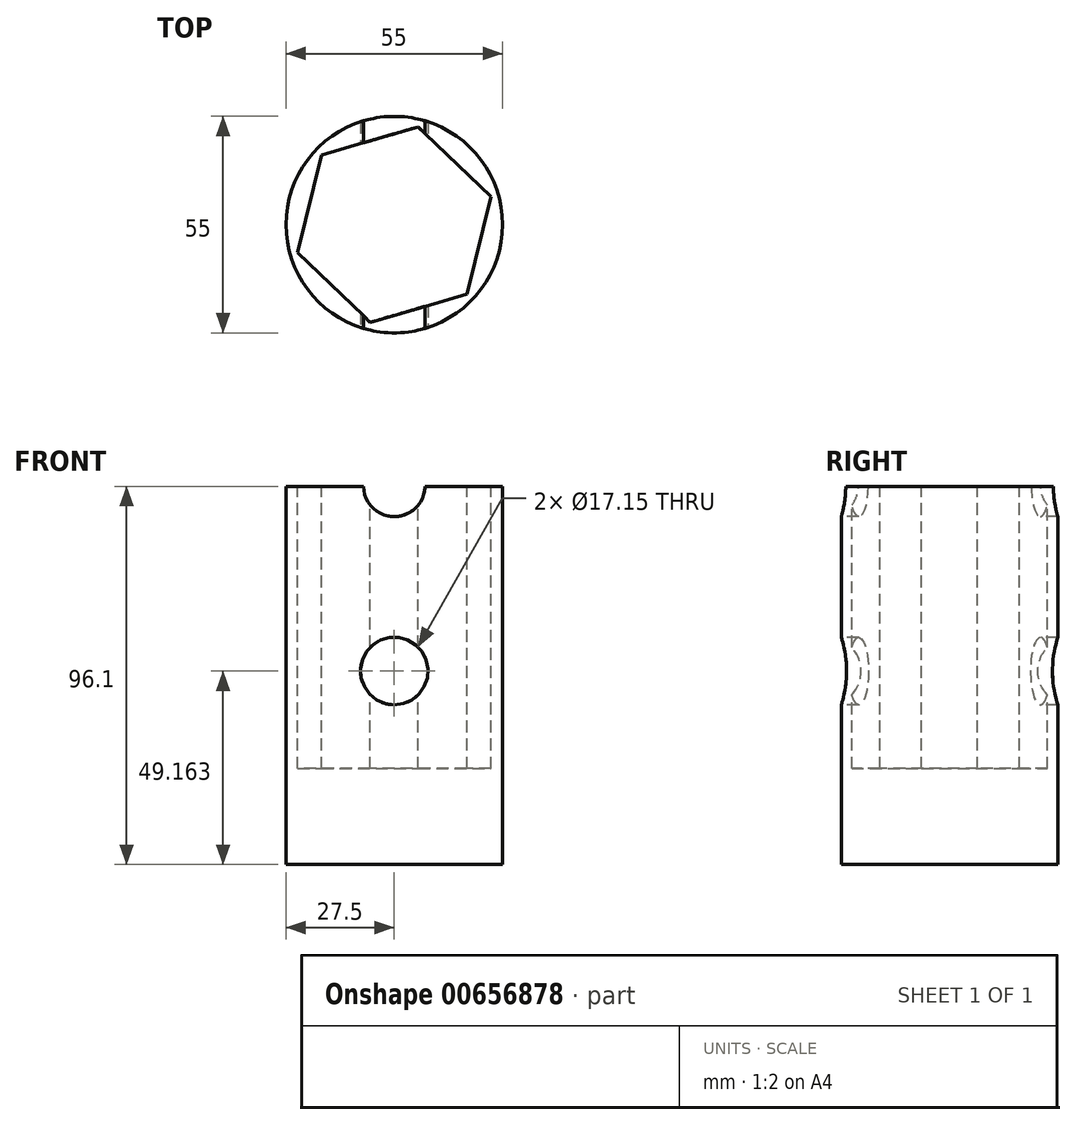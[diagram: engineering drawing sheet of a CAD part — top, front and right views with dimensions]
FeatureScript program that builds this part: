
annotation { "Feature Type Name" : "Feature", "Feature Type Description" : "" }
export const myFeature = defineFeature(function(context is Context, id is Id, definition is map)
    precondition{}
    {
        {
            var Q0;
            Q0=qCreatedBy(makeId("Top.planeOp"),FACE);
            var sketch = newSketch(context, id + "F0", { "sketchPlane" : qUnion([Q0])});
            skCircle(sketch, "E0", {"center": v(0, 0) * mm, "radius": 27.5 * mm});
            skSolve(sketch);
        }
        {
            var Q0;
            Q0=makeQuery(id+"F0.imprint","IMPRINT",FACE,{"disambiguationData":[TD([[makeQuery(id+"F0.imprint","IMPRINT",EDGE,{"derivedFrom":sQuery(id+"F0.wireOp",EDGE,"E0")}),1.0]])]});
            extrude(context, id + "F1", {"entities" : qUnion([Q0]), "depth" : 25 * mm, "offsetDistance" : 25 * mm});
        }
        {
            var Q0;
            Q0=makeQuery(id+"F1.opExtrude","CAP_FACE",FACE,{"disambiguationData":[OSD([sQuery(id+"F0.wireOp",EDGE,"E0")])],"isStart":false});
            extrude(context, id + "F2", {"entities" : qUnion([Q0]), "operationType" : NewBodyOperationType.ADD, "depth" : 71.1 * mm, "offsetDistance" : 25 * mm});
        }
        {
            var Q0;
            Q0=makeQuery(id+"F2.opExtrude","CAP_FACE",FACE,{"disambiguationData":[OSD([sQuery(id+"F0.wireOp",EDGE,"E0")])],"isStart":false});
            var sketch = newSketch(context, id + "F3", { "sketchPlane" : qUnion([Q0])});
            skCircle(sketch, "E1.cCircle", {"center": v(0, 0) * mm, "radius": 22.14 * mm, "construction": true});
            skLineSegment(sketch, "E1.0", {"start": v(18.45, -17.7) * mm, "end": v(-6.1, -24.83) * mm});
            skLineSegment(sketch, "E1.1", {"start": v(-6.1, -24.83) * mm, "end": v(-24.55, -7.13) * mm});
            skLineSegment(sketch, "E1.2", {"start": v(-24.55, -7.13) * mm, "end": v(-18.45, 17.7) * mm});
            skLineSegment(sketch, "E1.3", {"start": v(-18.45, 17.7) * mm, "end": v(6.1, 24.83) * mm});
            skLineSegment(sketch, "E1.4", {"start": v(6.1, 24.83) * mm, "end": v(24.55, 7.13) * mm});
            skLineSegment(sketch, "E1.5", {"start": v(24.55, 7.13) * mm, "end": v(18.45, -17.7) * mm});
            skPoint(sketch, "E1.0.midPoint", {"position": v(6.17, -21.26) * mm});
            skSolve(sketch);
        }
        {
            var Q0;
            Q0=makeQuery(id+"F3.imprint","IMPRINT",FACE,{"disambiguationData":[TD([[makeQuery(id+"F3.imprint","IMPRINT",EDGE,{"derivedFrom":sQuery(id+"F3.wireOp",EDGE,"E1.0")}),-1.0]])]});
            extrude(context, id + "F4", {"entities" : qUnion([Q0]), "operationType" : NewBodyOperationType.REMOVE, "oppositeDirection" : true, "depth" : 71.7 * mm, "offsetDistance" : 25 * mm});
        }
        {
            var Q0;
            Q0=qCreatedBy(makeId("Front.planeOp"),FACE);
            cPlane(context, id + "F5", {"entities" : qUnion([Q0]), "cplaneType" : CPlaneType.OFFSET, "offset" : 50 * mm, "width" : 150 * mm, "height" : 150 * mm});
        }
        {
            var Q0;
            Q0=qCreatedBy(id+"F5.planeOp",FACE);
            var sketch = newSketch(context, id + "F6", { "sketchPlane" : qUnion([Q0])});
            skCircle(sketch, "E2", {"center": v(0, 96.26) * mm, "radius": 7.83 * mm});
            skSolve(sketch);
        }
        {
            var Q0;
            Q0 = qSketchRegion(id + "F6", true);
            extrude(context, id + "F7", {"entities" : qUnion([Q0]), "operationType" : NewBodyOperationType.REMOVE, "oppositeDirection" : true, "depth" : 739.1 * mm, "offsetDistance" : 25 * mm});
        }
        {
            var Q0;
            Q0=qCreatedBy(id+"F5.planeOp",FACE);
            var sketch = newSketch(context, id + "F8", { "sketchPlane" : qUnion([Q0])});
            skCircle(sketch, "E3", {"center": v(0, 49.16) * mm, "radius": 8.57 * mm});
            skSolve(sketch);
        }
        {
            var Q0;
            Q0=makeQuery(id+"F8.imprint","IMPRINT",FACE,{"disambiguationData":[TD([[makeQuery(id+"F8.imprint","IMPRINT",EDGE,{"derivedFrom":sQuery(id+"F8.wireOp",EDGE,"E3")}),1.0]])]});
            extrude(context, id + "F9", {"entities" : qUnion([Q0]), "operationType" : NewBodyOperationType.REMOVE, "oppositeDirection" : true, "depth" : 106 * mm, "offsetDistance" : 25 * mm});
        }
    });
